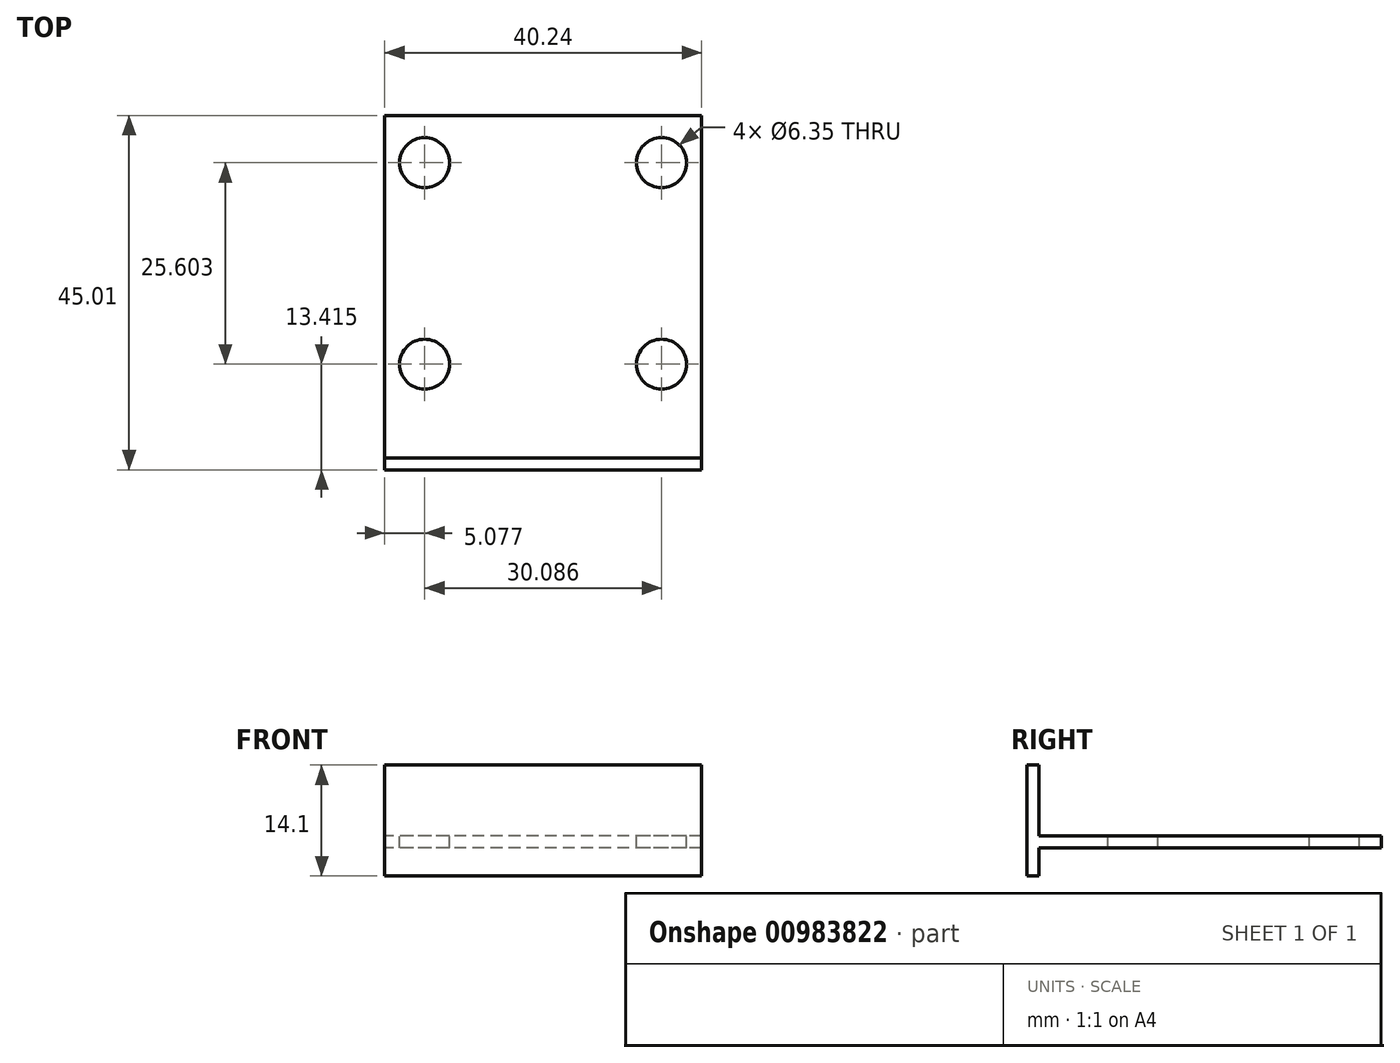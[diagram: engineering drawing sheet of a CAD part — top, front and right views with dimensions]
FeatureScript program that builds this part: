
annotation { "Feature Type Name" : "Feature", "Feature Type Description" : "" }
export const myFeature = defineFeature(function(context is Context, id is Id, definition is map)
    precondition{}
    {
        {
            var Q0;
            Q0=qCreatedBy(makeId("Top.planeOp"),FACE);
            var sketch = newSketch(context, id + "F0", { "sketchPlane" : qUnion([Q0])});
            skLineSegment(sketch, "E0.bottom", {"start": v(20.12, 21.74) * mm, "end": v(-20.12, 21.74) * mm});
            skLineSegment(sketch, "E0.top", {"start": v(20.12, -21.74) * mm, "end": v(-20.12, -21.74) * mm});
            skLineSegment(sketch, "E0.left", {"start": v(20.12, 21.74) * mm, "end": v(20.12, -21.74) * mm});
            skLineSegment(sketch, "E0.right", {"start": v(-20.12, 21.74) * mm, "end": v(-20.12, -21.74) * mm});
            skPoint(sketch, "E0.middle", {"position": v(0, 0) * mm});
            skSolve(sketch);
        }
        {
            var Q0;
            Q0 = qSketchRegion(id + "F0", true);
            extrude(context, id + "F1", {"entities" : qUnion([Q0]), "depth" : 1.52 * mm, "offsetDistance" : 25.4 * mm});
        }
        {
            var Q0;
            Q0=makeQuery(id+"F1.opExtrude","SWEPT_FACE",FACE,{"disambiguationData":[OSD([sQuery(id+"F0.wireOp",EDGE,"E0.top")])]});
            var sketch = newSketch(context, id + "F2", { "sketchPlane" : qUnion([Q0])});
            skLineSegment(sketch, "E1.bottom", {"start": v(20.12, -3.56) * mm, "end": v(-20.12, -3.56) * mm});
            skLineSegment(sketch, "E1.top", {"start": v(20.12, 10.54) * mm, "end": v(-20.12, 10.54) * mm});
            skLineSegment(sketch, "E1.left", {"start": v(20.12, -3.56) * mm, "end": v(20.12, 10.54) * mm});
            skLineSegment(sketch, "E1.right", {"start": v(-20.12, -3.56) * mm, "end": v(-20.12, 10.54) * mm});
            skPoint(sketch, "E1.middle", {"position": v(0, 3.5) * mm});
            skSolve(sketch);
        }
        {
            var Q0;
            Q0 = qSketchRegion(id + "F2", true);
            extrude(context, id + "F3", {"entities" : qUnion([Q0]), "operationType" : NewBodyOperationType.ADD, "depth" : 1.52 * mm, "offsetDistance" : 25.4 * mm});
        }
        {
            var Q0;
            Q0=makeQuery(id+"F1.opExtrude","CAP_FACE",FACE,{"disambiguationData":[OSD([sQuery(id+"F0.wireOp",EDGE,"E0.bottom"),sQuery(id+"F0.wireOp",EDGE,"E0.top"),sQuery(id+"F0.wireOp",EDGE,"E0.left"),sQuery(id+"F0.wireOp",EDGE,"E0.right")])],"isStart":false});
            var sketch = newSketch(context, id + "F4", { "sketchPlane" : qUnion([Q0])});
            skCircle(sketch, "E2", {"center": v(15.04, 15.75) * mm, "radius": 3.18 * mm});
            skCircle(sketch, "E3", {"center": v(15.04, -9.86) * mm, "radius": 3.18 * mm});
            skLineSegment(sketch, "E4", {"start": v(0, 21.74) * mm, "end": v(0, -21.74) * mm, "construction": true});
            skCircle(sketch, "E5.MirrorC", {"center": v(-15.04, 15.75) * mm, "radius": 3.18 * mm});
            skCircle(sketch, "E6.MirrorC", {"center": v(-15.04, -9.86) * mm, "radius": 3.18 * mm});
            skSolve(sketch);
        }
        {
            var Q0;
            Q0 = qSketchRegion(id + "F4", true);
            extrude(context, id + "F5", {"entities" : qUnion([Q0]), "operationType" : NewBodyOperationType.REMOVE, "oppositeDirection" : true, "depth" : 25.4 * mm, "offsetDistance" : 25.4 * mm});
        }
    });
